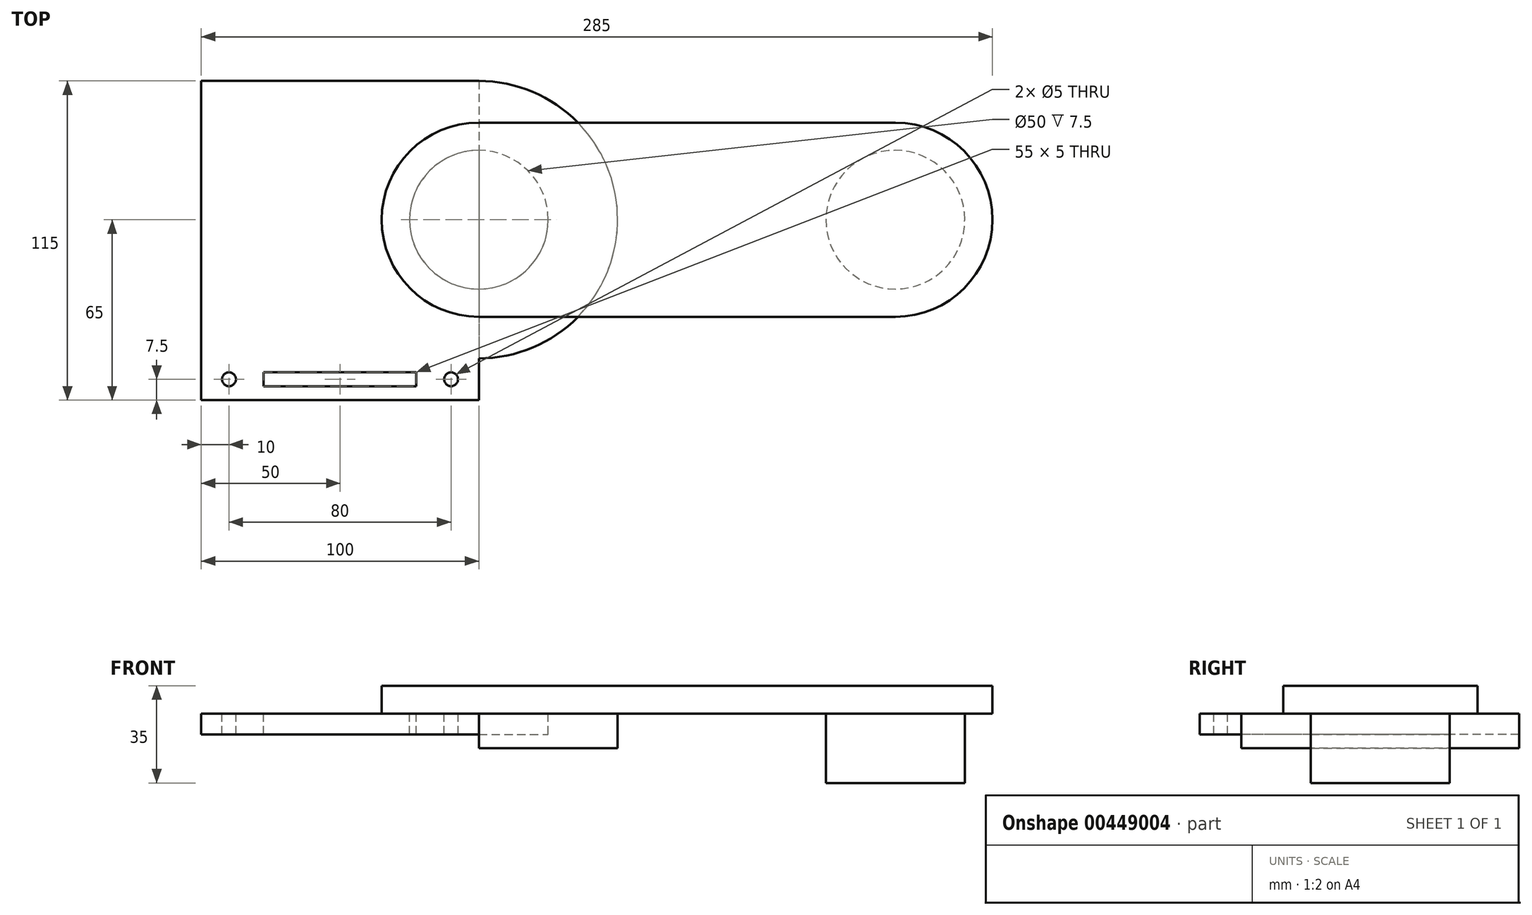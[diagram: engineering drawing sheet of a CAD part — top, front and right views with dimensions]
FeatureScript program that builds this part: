
annotation { "Feature Type Name" : "Feature", "Feature Type Description" : "" }
export const myFeature = defineFeature(function(context is Context, id is Id, definition is map)
    precondition{}
    {
        {
            var Q0;
            Q0=qCreatedBy(makeId("Top.planeOp"),FACE);
            var sketch = newSketch(context, id + "F0", { "sketchPlane" : qUnion([Q0])});
            skLineSegment(sketch, "E0.bottom", {"start": v(-50, 50) * mm, "end": v(50, 50) * mm});
            skLineSegment(sketch, "E0.top", {"start": v(-50, -50) * mm, "end": v(50, -50) * mm});
            skLineSegment(sketch, "E0.left", {"start": v(-50, 50) * mm, "end": v(-50, -50) * mm});
            skLineSegment(sketch, "E0.right", {"start": v(50, 50) * mm, "end": v(50, -50) * mm});
            skPoint(sketch, "E0.middle", {"position": v(0, 0) * mm});
            skCircle(sketch, "E1", {"center": v(50, 0) * mm, "radius": 50 * mm});
            skCircle(sketch, "E2", {"center": v(200, 0) * mm, "radius": 25 * mm});
            skSolve(sketch);
        }
        {
            var Q0;
            Q0=makeQuery(id+"F0.imprint","IMPRINT",FACE,{"disambiguationData":[TD([[makeQuery(id+"F0.imprint","IMPRINT",EDGE,{"derivedFrom":sQuery(id+"F0.wireOp",EDGE,"E2")}),1.0]])]});
            extrude(context, id + "F1", {"entities" : qUnion([Q0]), "endBound" : BoundingType.SYMMETRIC, "depth" : 25 * mm});
        }
        {
            var Q0;
            {var subQ0=sQuery(id+"F0.wireOp",EDGE,"E0.right");Q0=makeQuery(id+"F0.imprint","IMPRINT",FACE,{"disambiguationData":[TD([[makeQuery(id+"F0.imprint","IMPRINT",EDGE,{"derivedFrom":subQ0}),1.0]])]});}
            extrude(context, id + "F2", {"entities" : qUnion([Q0]), "depth" : 5 * mm});
        }
        {
            var Q0;
            {var subQ0=sQuery(id+"F0.wireOp",EDGE,"E0.right");Q0=makeQuery(id+"F0.imprint","IMPRINT",FACE,{"disambiguationData":[TD([[makeQuery(id+"F0.imprint","IMPRINT",EDGE,{"derivedFrom":subQ0}),-1.0]])]});}
            var Q1;
            {var subQ0=sQuery(id+"F0.wireOp",EDGE,"E0.bottom");Q1=makeQuery(id+"F0.imprint","IMPRINT",FACE,{"disambiguationData":[TD([[makeQuery(id+"F0.imprint","IMPRINT",EDGE,{"derivedFrom":subQ0}),-1.0]])]});}
            var Q2;
            {var subQ0=sQuery(id+"F0.wireOp",EDGE,"E0.right");Q2=makeQuery(id+"F0.imprint","IMPRINT",FACE,{"disambiguationData":[TD([[makeQuery(id+"F0.imprint","IMPRINT",EDGE,{"derivedFrom":subQ0}),1.0]])]});}
            var Q3;
            Q3=makeQuery(id+"F1.opExtrude","CAP_FACE",FACE,{"disambiguationData":[OSD([sQuery(id+"F0.wireOp",EDGE,"E2")])],"isStart":false});
            var Q4;
            Q4=makeQuery(id+"F2.opExtrude","CAP_FACE",FACE,{"disambiguationData":[OSD([sQuery(id+"F0.wireOp",EDGE,"E0.right"),sQuery(id+"F0.wireOp",EDGE,"E1")])],"isStart":false});
            extrude(context, id + "F3", {"entities" : qUnion([Q0, Q1, Q2]), "operationType" : NewBodyOperationType.ADD, "endBound" : BoundingType.UP_TO_SURFACE, "endBoundEntityFace" : qUnion([Q3]), "depth" : 25 * mm, "hasSecondDirection" : true, "secondDirectionBound" : SecondDirectionBoundingType.UP_TO_SURFACE, "secondDirectionOppositeDirection" : false, "secondDirectionBoundEntityFace" : qUnion([Q4]), "secondDirectionDepth" : 25 * mm});
        }
        {
            var Q0;
            Q0=makeQuery(id+"F3.opExtrude","SWEPT_FACE",FACE,{"disambiguationData":[OSD([sQuery(id+"F0.wireOp",EDGE,"E0.top")])]});
            extrude(context, id + "F4", {"entities" : qUnion([Q0]), "operationType" : NewBodyOperationType.ADD, "depth" : 15 * mm});
        }
        {
            var Q0;
            {var subQ0=sQuery(id+"F0.wireOp",EDGE,"E2");Q0=makeQuery(id+"F4.boolean.opBoolean","MERGE",FACE,{"derivedFrom":[makeQuery(id+"F3.opExtrude","CAP_FACE",FACE,{"disambiguationData":[OSD([subQ0])],"isStart":false}),makeQuery(id+"F4.opExtrude","SWEPT_FACE",FACE,{"disambiguationData":[OSD([sQuery(id+"F0.wireOp",EDGE,"E0.top"),subQ0])]})]});}
            var sketch = newSketch(context, id + "F5", { "sketchPlane" : qUnion([Q0])});
            skLineSegment(sketch, "E3.bottom", {"start": v(-27.5, -55) * mm, "end": v(27.5, -55) * mm});
            skLineSegment(sketch, "E3.top", {"start": v(-27.5, -60) * mm, "end": v(27.5, -60) * mm});
            skLineSegment(sketch, "E3.left", {"start": v(-27.5, -55) * mm, "end": v(-27.5, -60) * mm});
            skLineSegment(sketch, "E3.right", {"start": v(27.5, -55) * mm, "end": v(27.5, -60) * mm});
            skPoint(sketch, "E3.middle", {"position": v(0, -57.5) * mm});
            skPoint(sketch, "E3.middle.positionSnap0", {"position": v(0, -65) * mm});
            skPoint(sketch, "E3.centerSnap0", {"position": v(0, -65) * mm});
            skCircle(sketch, "E4", {"center": v(40, -57.5) * mm, "radius": 2.5 * mm});
            skPoint(sketch, "E5", {"position": v(50, -57.5) * mm});
            skLineSegment(sketch, "E6", {"start": v(0, -60) * mm, "end": v(0, -55) * mm, "construction": true});
            skCircle(sketch, "E7.MirrorC", {"center": v(-40, -57.5) * mm, "radius": 2.5 * mm});
            skSolve(sketch);
        }
        {
            var Q0;
            Q0 = qSketchRegion(id + "F5", true);
            extrude(context, id + "F6", {"entities" : qUnion([Q0]), "operationType" : NewBodyOperationType.REMOVE, "endBound" : BoundingType.THROUGH_ALL, "oppositeDirection" : true, "depth" : 25 * mm});
        }
        {
            var Q0;
            Q0=makeQuery(id+"F1.opExtrude","CAP_FACE",FACE,{"disambiguationData":[OSD([sQuery(id+"F0.wireOp",EDGE,"E2")])],"isStart":false});
            var sketch = newSketch(context, id + "F7", { "sketchPlane" : qUnion([Q0])});
            skCircle(sketch, "E8", {"center": v(200, 0) * mm, "radius": 35 * mm});
            skPoint(sketch, "E9.0", {"position": v(50, 0) * mm});
            skCircle(sketch, "E10", {"center": v(50, 0) * mm, "radius": 35 * mm});
            skCircle(sketch, "E11", {"center": v(50, 0) * mm, "radius": 25 * mm});
            skLineSegment(sketch, "E12", {"start": v(50, 35) * mm, "end": v(200, 35) * mm});
            skLineSegment(sketch, "E13", {"start": v(50, -35) * mm, "end": v(200, -35) * mm});
            skSolve(sketch);
        }
        {
            var Q0;
            Q0=makeQuery(id+"F7.imprint","IMPRINT",FACE,{"disambiguationData":[TD([[makeQuery(id+"F7.imprint","IMPRINT",EDGE,{"derivedFrom":makeQuery(id+"F1.opExtrude","CAP_EDGE",EDGE,{"disambiguationData":[OSD([sQuery(id+"F0.wireOp",EDGE,"E2")])],"isStart":false})}),-1.0]])]});
            var Q1;
            {var subQ0=sQuery(id+"F7.wireOp",EDGE,"E12");Q1=makeQuery(id+"F7.imprint","IMPRINT",FACE,{"disambiguationData":[TD([[makeQuery(id+"F7.imprint","IMPRINT",EDGE,{"derivedFrom":subQ0}),-1.0]])]});}
            var Q2;
            Q2=makeQuery(id+"F7.imprint","IMPRINT",FACE,{"disambiguationData":[TD([[makeQuery(id+"F7.imprint","IMPRINT",EDGE,{"derivedFrom":sQuery(id+"F7.wireOp",EDGE,"E11")}),-1.0]])]});
            var Q3;
            Q3=makeQuery(id+"F7.imprint","IMPRINT",FACE,{"disambiguationData":[TD([[makeQuery(id+"F7.imprint","IMPRINT",EDGE,{"derivedFrom":sQuery(id+"F7.wireOp",EDGE,"E11")}),1.0]])]});
            var Q4;
            Q4=makeQuery(id+"F1.opExtrude","CAP_FACE",FACE,{"disambiguationData":[OSD([sQuery(id+"F0.wireOp",EDGE,"E2")])],"isStart":false});
            extrude(context, id + "F8", {"entities" : qUnion([Q0, Q1, Q2, Q3, Q4]), "operationType" : NewBodyOperationType.ADD, "depth" : 10 * mm});
        }
        {
            var Q0;
            Q0=makeQuery(id+"F7.imprint","IMPRINT",FACE,{"disambiguationData":[TD([[makeQuery(id+"F7.imprint","IMPRINT",EDGE,{"derivedFrom":sQuery(id+"F7.wireOp",EDGE,"E11")}),1.0]])]});
            var Q1;
            {var subQ0=sQuery(id+"F0.wireOp",EDGE,"E1");var subQ1=sQuery(id+"F0.wireOp",EDGE,"E0.right");Q1=makeQuery(id+"F4.boolean.opBoolean","MERGE",FACE,{"derivedFrom":[makeQuery(id+"F3.opExtrude","CAP_FACE",FACE,{"disambiguationData":[OSD([subQ1,subQ0])],"isStart":true}),makeQuery(id+"F4.opExtrude","SWEPT_FACE",FACE,{"disambiguationData":[OSD([sQuery(id+"F0.wireOp",EDGE,"E0.top"),subQ1,subQ0])]})]});}
            extrude(context, id + "F9", {"entities" : qUnion([Q0]), "operationType" : NewBodyOperationType.ADD, "endBound" : BoundingType.UP_TO_SURFACE, "oppositeDirection" : true, "endBoundEntityFace" : qUnion([Q1]), "depth" : 25 * mm});
        }
        {
            var Q0;
            Q0=makeQuery(id+"F7.imprint","IMPRINT",FACE,{"disambiguationData":[TD([[makeQuery(id+"F7.imprint","IMPRINT",EDGE,{"derivedFrom":sQuery(id+"F7.wireOp",EDGE,"E11")}),1.0]])]});
            var Q1;
            {var subQ0=sQuery(id+"F0.wireOp",EDGE,"E1");var subQ1=sQuery(id+"F0.wireOp",EDGE,"E0.right");Q1=makeQuery(id+"F4.boolean.opBoolean","MERGE",FACE,{"derivedFrom":[makeQuery(id+"F3.opExtrude","CAP_FACE",FACE,{"disambiguationData":[OSD([subQ1,subQ0])],"isStart":true}),makeQuery(id+"F4.opExtrude","SWEPT_FACE",FACE,{"disambiguationData":[OSD([sQuery(id+"F0.wireOp",EDGE,"E0.top"),subQ1,subQ0])]})]});}
            extrude(context, id + "F10", {"entities" : qUnion([Q0]), "operationType" : NewBodyOperationType.REMOVE, "endBound" : BoundingType.UP_TO_SURFACE, "oppositeDirection" : true, "endBoundEntityFace" : qUnion([Q1]), "depth" : 25 * mm});
        }
    });
